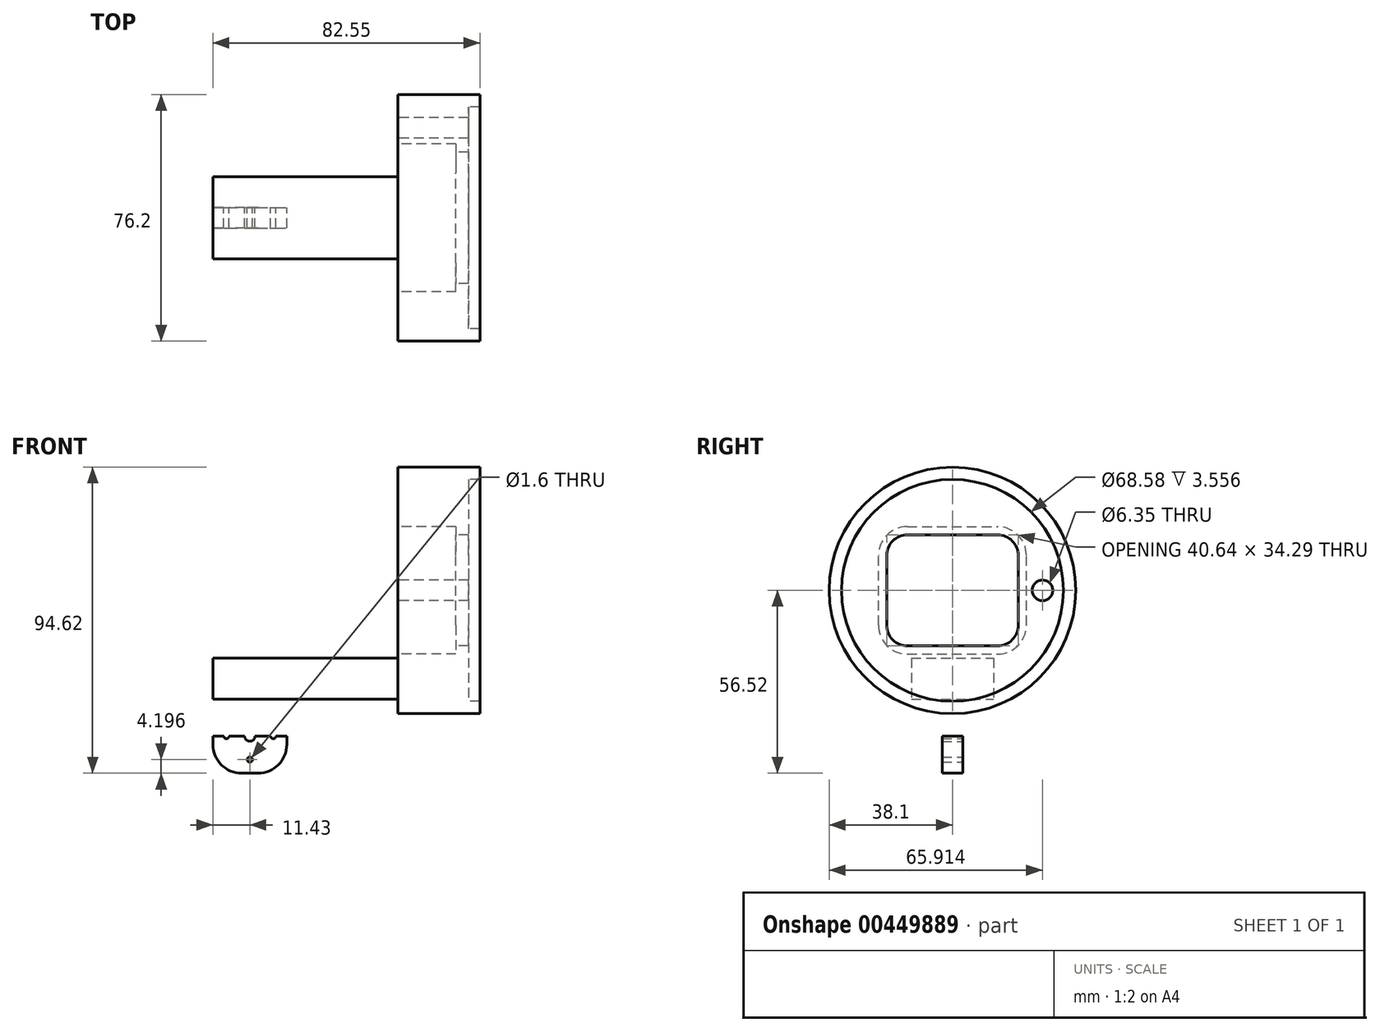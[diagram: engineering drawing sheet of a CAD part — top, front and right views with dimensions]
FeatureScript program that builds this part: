
annotation { "Feature Type Name" : "Feature", "Feature Type Description" : "" }
export const myFeature = defineFeature(function(context is Context, id is Id, definition is map)
    precondition{}
    {
        {
            var Q0;
            Q0=qCreatedBy(makeId("Front.planeOp"),FACE);
            var sketch = newSketch(context, id + "F0", { "sketchPlane" : qUnion([Q0])});
            skLineSegment(sketch, "E0.bottom", {"start": v(32.82, 38.1) * mm, "end": v(58.22, 38.1) * mm});
            skLineSegment(sketch, "E0.top", {"start": v(32.82, -38.1) * mm, "end": v(58.22, -38.1) * mm});
            skLineSegment(sketch, "E0.left", {"start": v(32.82, 38.1) * mm, "end": v(32.82, -38.1) * mm});
            skLineSegment(sketch, "E0.right", {"start": v(58.22, 38.1) * mm, "end": v(58.22, -38.1) * mm});
            skPoint(sketch, "E0.middle", {"position": v(45.52, 0) * mm});
            skLineSegment(sketch, "E1.bottom", {"start": v(58.22, 34.3) * mm, "end": v(54.66, 34.3) * mm});
            skLineSegment(sketch, "E1.top", {"start": v(58.22, -34.3) * mm, "end": v(54.66, -34.3) * mm});
            skLineSegment(sketch, "E1.left", {"start": v(58.22, 34.3) * mm, "end": v(58.22, -34.3) * mm});
            skLineSegment(sketch, "E1.right", {"start": v(54.66, 34.3) * mm, "end": v(54.66, -34.3) * mm});
            skPoint(sketch, "E1.middle", {"position": v(56.44, 0) * mm});
            skLineSegment(sketch, "E2", {"start": v(32.82, 0) * mm, "end": v(58.22, 0) * mm});
            skLineSegment(sketch, "E3", {"start": v(32.82, -20.96) * mm, "end": v(-24.33, -20.96) * mm});
            skLineSegment(sketch, "E4", {"start": v(32.82, -33.66) * mm, "end": v(-24.33, -33.66) * mm});
            skLineSegment(sketch, "E5", {"start": v(-24.33, -20.96) * mm, "end": v(-24.33, -33.66) * mm});
            skLineSegment(sketch, "E6.bottom", {"start": v(-1.47, -56.52) * mm, "end": v(-24.33, -56.52) * mm});
            skLineSegment(sketch, "E6.top", {"start": v(-1.47, -33.66) * mm, "end": v(-24.33, -33.66) * mm});
            skLineSegment(sketch, "E6.left", {"start": v(-1.47, -56.52) * mm, "end": v(-1.47, -33.66) * mm});
            skLineSegment(sketch, "E6.right", {"start": v(-24.33, -56.52) * mm, "end": v(-24.33, -33.66) * mm});
            skPoint(sketch, "E6.middle", {"position": v(-12.9, -45.09) * mm});
            skCircle(sketch, "E7", {"center": v(-12.9, -45.09) * mm, "radius": 1.59 * mm});
            skLineSegment(sketch, "E8", {"start": v(-12.9, -45.09) * mm, "end": v(-1.47, -45.09) * mm});
            skLineSegment(sketch, "E9", {"start": v(-1.47, -45.09) * mm, "end": v(-24.33, -45.09) * mm});
            skCircle(sketch, "E10", {"center": v(-20.14, -45.09) * mm, "radius": 0.8 * mm});
            skCircle(sketch, "E11", {"center": v(-5.66, -45.09) * mm, "radius": 0.8 * mm});
            skLineSegment(sketch, "E12", {"start": v(-12.9, -38.01) * mm, "end": v(-12.9, -56.52) * mm});
            skCircle(sketch, "E13", {"center": v(-12.9, -37.85) * mm, "radius": 0.8 * mm});
            skCircle(sketch, "E14", {"center": v(-12.9, -52.32) * mm, "radius": 0.8 * mm});
            skSolve(sketch);
        }
        {
            var Q0;
            {var subQ2=sQuery(id+"F0.wireOp",EDGE,"E0.bottom");Q0=makeQuery(id+"F0.imprint","IMPRINT",FACE,{"disambiguationData":[TD([[makeQuery(id+"F0.imprint","IMPRINT",EDGE,{"derivedFrom":subQ2}),-1.0]])]});}
            var Q1;
            Q1=sQuery(id+"F0.wireOp",EDGE,"E2");
            revolve(context, id + "F1", {"entities" : qUnion([Q0]), "axis" : qUnion([Q1]), "revolveType" : RevolveType.FULL});
        }
        {
            var Q0;
            Q0=qCreatedBy(makeId("Right.planeOp"),FACE);
            var sketch = newSketch(context, id + "F2", { "sketchPlane" : qUnion([Q0])});
            skArc(sketch, "E15.0", {"start": v(-13.97, 19.69) * mm, "mid": v(-20.26, 17.08) * mm, "end": v(-22.86, 10.8) * mm});
            skLineSegment(sketch, "E15.1", {"start": v(-22.86, -10.8) * mm, "end": v(-22.86, 10.8) * mm});
            skArc(sketch, "E15.3", {"start": v(-22.86, -10.8) * mm, "mid": v(-20.26, -17.08) * mm, "end": v(-13.97, -19.69) * mm});
            skArc(sketch, "E15.4", {"start": v(22.86, 10.8) * mm, "mid": v(20.26, 17.08) * mm, "end": v(13.97, 19.69) * mm});
            skLineSegment(sketch, "E15.5", {"start": v(22.86, -10.8) * mm, "end": v(22.86, 10.8) * mm});
            skArc(sketch, "E15.6", {"start": v(13.97, -19.69) * mm, "mid": v(20.26, -17.08) * mm, "end": v(22.86, -10.8) * mm});
            skLineSegment(sketch, "E15.7", {"start": v(-13.97, -19.69) * mm, "end": v(13.97, -19.69) * mm});
            skPoint(sketch, "E16", {"position": v(27.81, 0) * mm});
            skLineSegment(sketch, "E17", {"start": v(-22.86, 10.8) * mm, "end": v(-22.86, -10.8) * mm});
            skLineSegment(sketch, "E18", {"start": v(-13.97, 19.69) * mm, "end": v(13.97, 19.69) * mm});
            skLineSegment(sketch, "E19", {"start": v(22.86, 10.8) * mm, "end": v(22.86, -10.8) * mm});
            skArc(sketch, "E20", {"start": v(18.97, -18.15) * mm, "mid": v(16.58, -19.3) * mm, "end": v(13.97, -19.69) * mm});
            skCircle(sketch, "E21", {"center": v(27.81, 0) * mm, "radius": 3.18 * mm});
            skSolve(sketch);
        }
        {
            var Q0;
            {var subQ0=sQuery(id+"F0.wireOp",EDGE,"E3");Q0=makeQuery(id+"F0.imprint","IMPRINT",FACE,{"disambiguationData":[TD([[makeQuery(id+"F0.imprint","IMPRINT",EDGE,{"derivedFrom":subQ0}),1.0]])]});}
            extrude(context, id + "F3", {"entities" : qUnion([Q0]), "operationType" : NewBodyOperationType.ADD, "endBound" : BoundingType.SYMMETRIC, "depth" : 25.4 * mm});
        }
        {
            var Q0;
            Q0=makeQuery(id+"F0.imprint","IMPRINT",FACE,{"disambiguationData":[TD([[makeQuery(id+"F0.imprint","IMPRINT",EDGE,{"derivedFrom":sQuery(id+"F0.wireOp",EDGE,"E6.bottom")}),-1.0]])]});
            var Q1;
            {var subQ1=sQuery(id+"F0.wireOp",EDGE,"E6.top");Q1=makeQuery(id+"F0.imprint","IMPRINT",FACE,{"disambiguationData":[TD([[makeQuery(id+"F0.imprint","IMPRINT",EDGE,{"derivedFrom":subQ1}),1.0]])]});}
            extrude(context, id + "F4", {"entities" : qUnion([Q0, Q1]), "operationType" : NewBodyOperationType.ADD, "endBound" : BoundingType.SYMMETRIC, "depth" : 6.35 * mm});
        }
        {
            var Q0;
            Q0=makeQuery(id+"F4.opExtrude","SWEPT_EDGE",EDGE,{"disambiguationData":[OSD([sQuery(id+"F0.wireOp",EDGE,"E6.bottom"),sQuery(id+"F0.wireOp",EDGE,"E6.right")])]});
            var Q1;
            Q1=makeQuery(id+"F4.opExtrude","SWEPT_EDGE",EDGE,{"disambiguationData":[OSD([sQuery(id+"F0.wireOp",EDGE,"E6.bottom"),sQuery(id+"F0.wireOp",EDGE,"E6.left")])]});
            fillet(context, id + "F5", {"entities" : qUnion([Q0, Q1]), "radius" : 8.9 * mm, "tangentPropagation" : true, "allowEdgeOverflow" : false});
        }
        {
            var Q0;
            Q0=qCreatedBy(makeId("Right.planeOp"),FACE);
            var sketch = newSketch(context, id + "F6", { "sketchPlane" : qUnion([Q0])});
            skArc(sketch, "E22.0", {"start": v(-13.97, 17.15) * mm, "mid": v(-18.46, 15.29) * mm, "end": v(-20.32, 10.8) * mm});
            skLineSegment(sketch, "E22.1", {"start": v(-20.32, -10.8) * mm, "end": v(-20.32, 10.8) * mm});
            skLineSegment(sketch, "E22.2", {"start": v(-13.97, 17.15) * mm, "end": v(13.97, 17.15) * mm});
            skArc(sketch, "E22.3", {"start": v(-20.32, -10.8) * mm, "mid": v(-18.46, -15.29) * mm, "end": v(-13.97, -17.15) * mm});
            skArc(sketch, "E22.4", {"start": v(20.32, 10.8) * mm, "mid": v(18.46, 15.29) * mm, "end": v(13.97, 17.15) * mm});
            skLineSegment(sketch, "E22.5", {"start": v(20.32, -10.8) * mm, "end": v(20.32, 10.8) * mm});
            skArc(sketch, "E22.6", {"start": v(13.97, -17.15) * mm, "mid": v(18.46, -15.29) * mm, "end": v(20.32, -10.8) * mm});
            skLineSegment(sketch, "E22.7", {"start": v(-13.97, -17.15) * mm, "end": v(13.97, -17.15) * mm});
            skSolve(sketch);
        }
        {
            var Q0;
            Q0=makeQuery(id+"F2.imprint","IMPRINT",FACE,{"disambiguationData":[TD([[makeQuery(id+"F2.imprint","IMPRINT",EDGE,{"derivedFrom":sQuery(id+"F2.wireOp",EDGE,"E15.0")}),1.0]])]});
            extrude(context, id + "F7", {"entities" : qUnion([Q0]), "operationType" : NewBodyOperationType.REMOVE, "depth" : 50.8 * mm});
        }
        {
            var Q0;
            Q0=makeQuery(id+"F6.imprint","IMPRINT",FACE,{"disambiguationData":[TD([[makeQuery(id+"F6.imprint","IMPRINT",EDGE,{"derivedFrom":sQuery(id+"F6.wireOp",EDGE,"E22.0")}),1.0]])]});
            extrude(context, id + "F8", {"entities" : qUnion([Q0]), "operationType" : NewBodyOperationType.REMOVE, "depth" : 57.15 * mm});
        }
        {
            var Q0;
            Q0=makeQuery(id+"F2.imprint","IMPRINT",FACE,{"disambiguationData":[TD([[makeQuery(id+"F2.imprint","IMPRINT",EDGE,{"derivedFrom":sQuery(id+"F2.wireOp",EDGE,"E21")}),1.0]])]});
            extrude(context, id + "F9", {"entities" : qUnion([Q0]), "operationType" : NewBodyOperationType.REMOVE, "depth" : 76.2 * mm});
        }
    });
